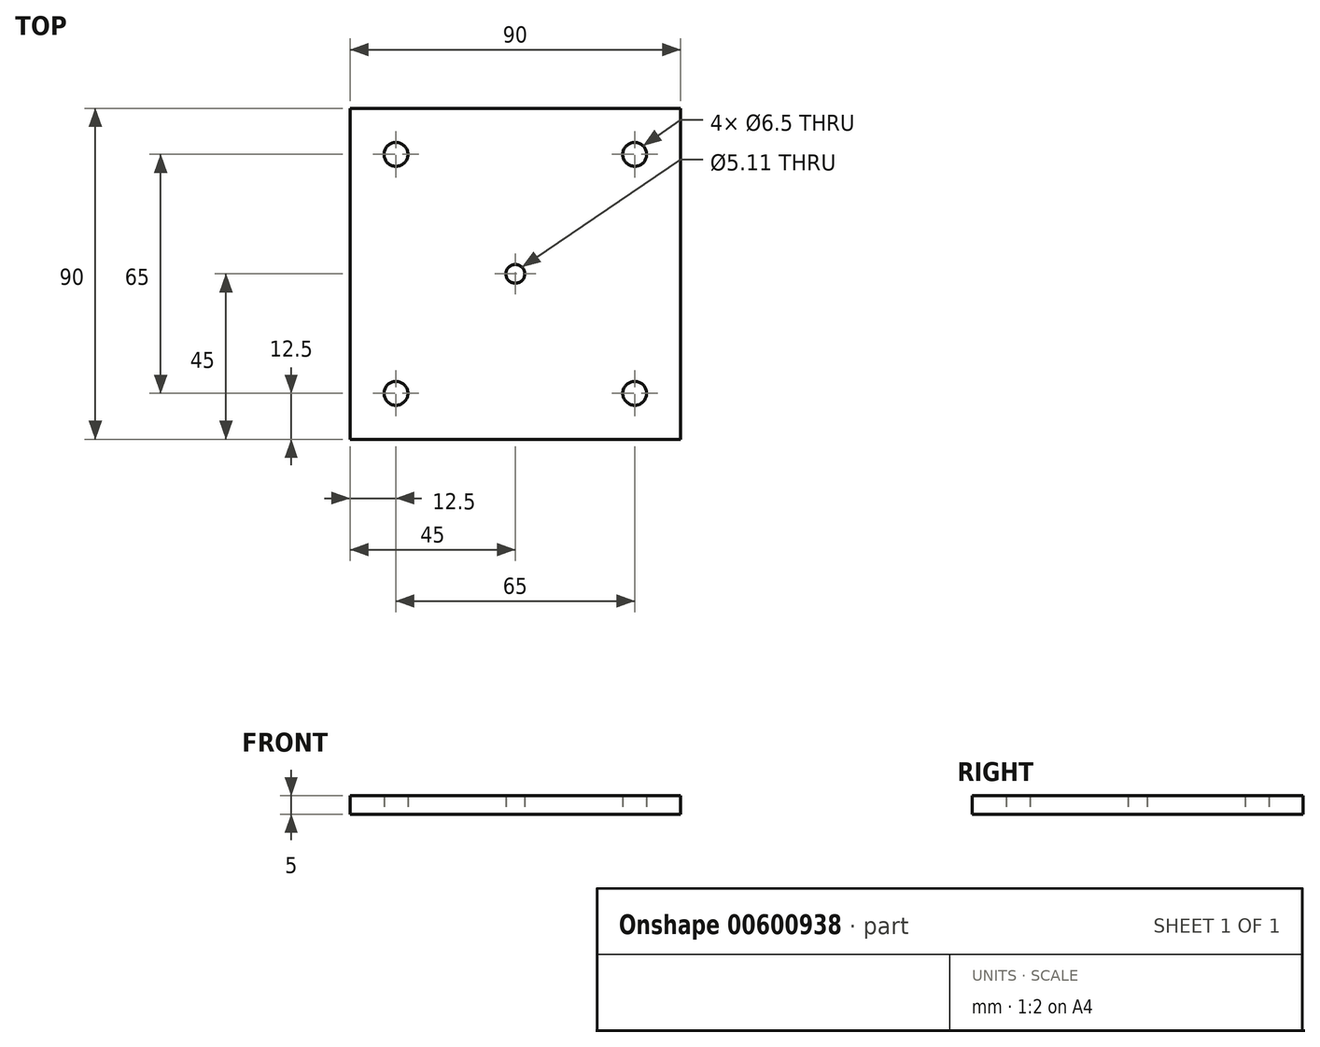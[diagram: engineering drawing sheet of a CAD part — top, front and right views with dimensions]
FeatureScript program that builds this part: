
annotation { "Feature Type Name" : "Feature", "Feature Type Description" : "" }
export const myFeature = defineFeature(function(context is Context, id is Id, definition is map)
    precondition{}
    {
        {
            var Q0;
            Q0=qCreatedBy(makeId("Top.planeOp"),FACE);
            var sketch = newSketch(context, id + "F0", { "sketchPlane" : qUnion([Q0])});
            skLineSegment(sketch, "E0.bottom", {"start": v(45, 45) * mm, "end": v(-45, 45) * mm});
            skLineSegment(sketch, "E0.top", {"start": v(45, -45) * mm, "end": v(-45, -45) * mm});
            skLineSegment(sketch, "E0.left", {"start": v(45, 45) * mm, "end": v(45, -45) * mm});
            skLineSegment(sketch, "E0.right", {"start": v(-45, 45) * mm, "end": v(-45, -45) * mm});
            skPoint(sketch, "E0.middle", {"position": v(0, 0) * mm});
            skPoint(sketch, "E1", {"position": v(-32.5, 32.5) * mm});
            skPoint(sketch, "E2", {"position": v(32.5, 32.5) * mm});
            skPoint(sketch, "E3", {"position": v(32.5, -32.5) * mm});
            skPoint(sketch, "E4", {"position": v(-32.5, -32.5) * mm});
            skSolve(sketch);
        }
        {
            var Q0;
            Q0=makeQuery(id+"F0.imprint","IMPRINT",FACE,{"disambiguationData":[TD([[makeQuery(id+"F0.imprint","IMPRINT",EDGE,{"derivedFrom":sQuery(id+"F0.wireOp",EDGE,"E0.bottom")}),1.0]])]});
            extrude(context, id + "F1", {"entities" : qUnion([Q0]), "depth" : 5 * mm, "offsetDistance" : 25 * mm});
        }
        {
            var Q0;
            Q0=sQuery(id+"F0.wireOp",VERTEX,"E1");
            var Q1;
            Q1=sQuery(id+"F0.wireOp",VERTEX,"E2");
            var Q2;
            Q2=sQuery(id+"F0.wireOp",VERTEX,"E3");
            var Q3;
            Q3=sQuery(id+"F0.wireOp",VERTEX,"E4");
            var Q4;
            Q4=makeQuery(id+"F1.opExtrude","SWEPT_BODY",BODY,{"disambiguationData":[OSD([sQuery(id+"F0.wireOp",EDGE,"E0.bottom"),sQuery(id+"F0.wireOp",EDGE,"E0.top"),sQuery(id+"F0.wireOp",EDGE,"E0.left"),sQuery(id+"F0.wireOp",EDGE,"E0.right")])]});
            hole(context, id + "F2", {"style" : HoleStyle.SIMPLE, "endStyle" : HoleEndStyle.THROUGH, "oppositeDirection" : true, "standardTappedOrClearance" : lookupTablePath({ "standard" : "ISO", "size" : "6.5", "type" : "Drilled" }), "standardBlindInLast" : lookupTablePath({ "standard" : "ISO", "size" : "6.5", "type" : "Drilled" }), "holeDiameter" : 6.5 * mm, "isTappedThrough" : true, "tappedDepth" : 3.5 * mm, "tapClearance" : 3, "locations" : qUnion([Q0, Q1, Q2, Q3]), "scope" : qUnion([Q4])});
        }
        {
            var Q0;
            Q0=sQuery(id+"F0.wireOp",VERTEX,"E0.middle");
            var Q1;
            Q1=makeQuery(id+"F1.opExtrude","SWEPT_BODY",BODY,{"disambiguationData":[OSD([sQuery(id+"F0.wireOp",EDGE,"E0.bottom"),sQuery(id+"F0.wireOp",EDGE,"E0.top"),sQuery(id+"F0.wireOp",EDGE,"E0.left"),sQuery(id+"F0.wireOp",EDGE,"E0.right")])]});
            hole(context, id + "F3", {"style" : HoleStyle.SIMPLE, "endStyle" : HoleEndStyle.THROUGH, "oppositeDirection" : true, "standardTappedOrClearance" : lookupTablePath({ "standard" : "ANSI", "engagement" : "75%", "pitch" : "20 tpi", "size" : "1/4", "type" : "Tapped" }), "standardBlindInLast" : lookupTablePath({ "standard" : "ANSI", "engagement" : "75%", "pitch" : "20 tpi", "size" : "1/4", "type" : "Tapped" }), "holeDiameter" : 5.1 * mm, "showTappedDepth" : true, "isTappedThrough" : true, "tappedDepth" : 3.5 * mm, "tapClearance" : 3, "locations" : qUnion([Q0]), "scope" : qUnion([Q1]), "majorDiameter" : 6.35 * mm});
        }
    });
